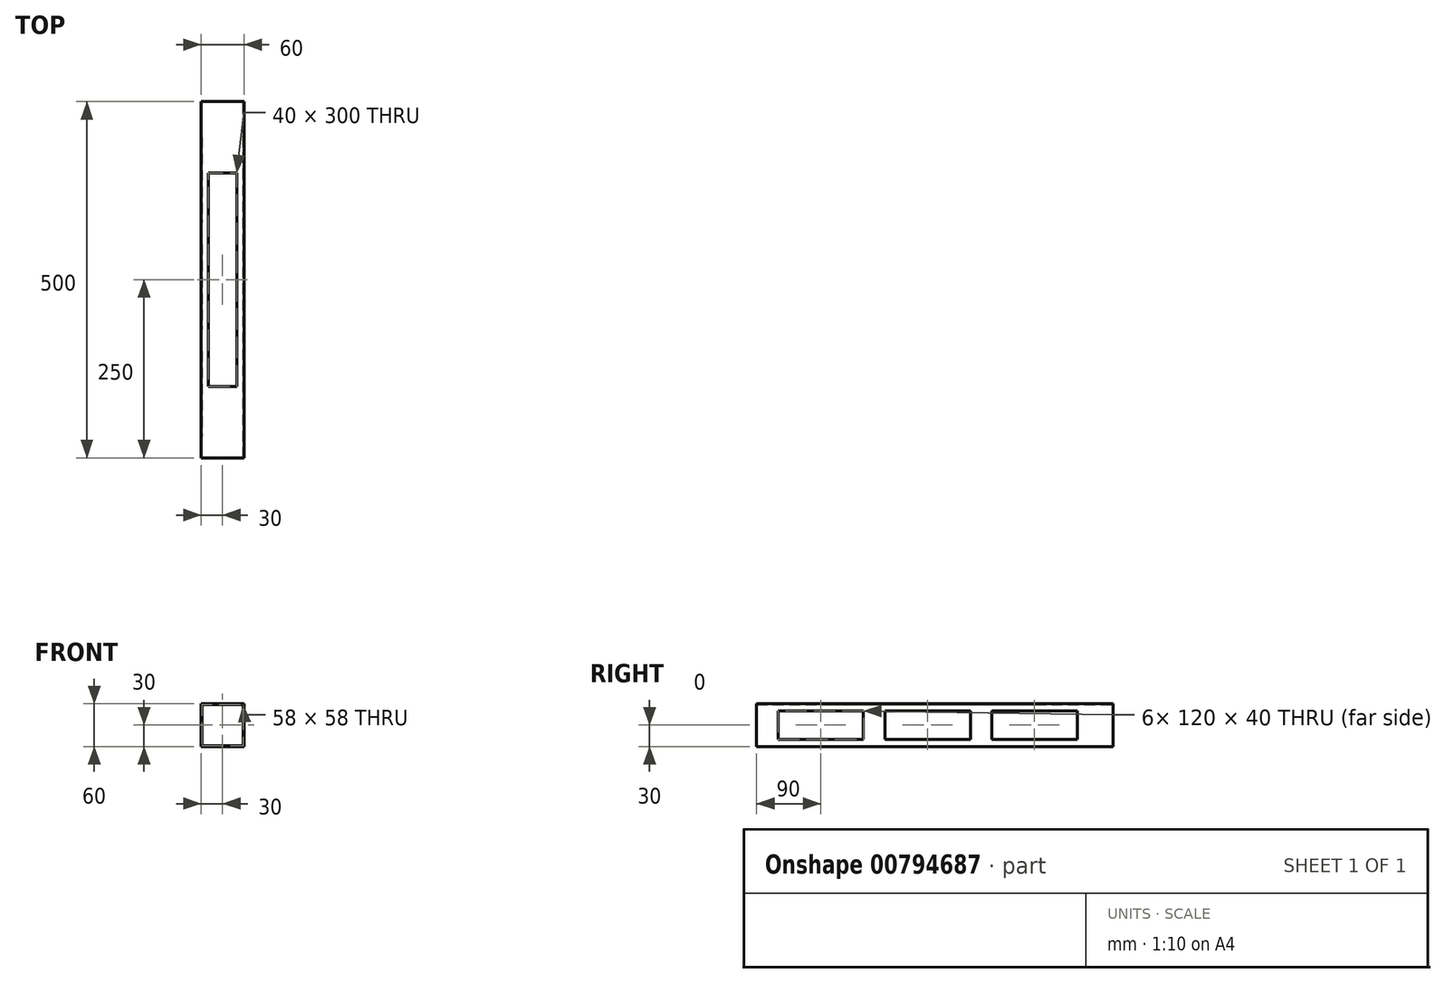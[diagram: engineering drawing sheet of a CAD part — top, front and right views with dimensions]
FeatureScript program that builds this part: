
annotation { "Feature Type Name" : "Feature", "Feature Type Description" : "" }
export const myFeature = defineFeature(function(context is Context, id is Id, definition is map)
    precondition{}
    {
        {
            var Q0;
            Q0=qCreatedBy(makeId("Front.planeOp"),FACE);
            var sketch = newSketch(context, id + "F0", { "sketchPlane" : qUnion([Q0])});
            skLineSegment(sketch, "E0.bottom", {"start": v(-30, -30) * mm, "end": v(30, -30) * mm});
            skLineSegment(sketch, "E0.top", {"start": v(-30, 30) * mm, "end": v(30, 30) * mm});
            skLineSegment(sketch, "E0.left", {"start": v(-30, -30) * mm, "end": v(-30, 30) * mm});
            skLineSegment(sketch, "E0.right", {"start": v(30, -30) * mm, "end": v(30, 30) * mm});
            skPoint(sketch, "E0.middle", {"position": v(0, 0) * mm});
            skLineSegment(sketch, "E1.bottom", {"start": v(-29, -29) * mm, "end": v(29, -29) * mm});
            skLineSegment(sketch, "E1.top", {"start": v(-29, 29) * mm, "end": v(29, 29) * mm});
            skLineSegment(sketch, "E1.left", {"start": v(-29, -29) * mm, "end": v(-29, 29) * mm});
            skLineSegment(sketch, "E1.right", {"start": v(29, -29) * mm, "end": v(29, 29) * mm});
            skSolve(sketch);
        }
        {
            var Q0;
            Q0=makeQuery(id+"F0.imprint","IMPRINT",FACE,{"disambiguationData":[TD([[makeQuery(id+"F0.imprint","IMPRINT",EDGE,{"derivedFrom":sQuery(id+"F0.wireOp",EDGE,"E0.bottom")}),1.0]])]});
            extrude(context, id + "F1", {"entities" : qUnion([Q0]), "depth" : 500 * mm, "offsetDistance" : 25 * mm});
        }
        {
            var Q0;
            Q0=makeQuery(id+"F1.opExtrude","SWEPT_FACE",FACE,{"disambiguationData":[OSD([sQuery(id+"F0.wireOp",EDGE,"E0.right")])]});
            var sketch = newSketch(context, id + "F2", { "sketchPlane" : qUnion([Q0])});
            skLineSegment(sketch, "E2.bottom", {"start": v(-470, 20) * mm, "end": v(-350, 20) * mm});
            skLineSegment(sketch, "E2.top", {"start": v(-470, -20) * mm, "end": v(-350, -20) * mm});
            skLineSegment(sketch, "E2.left", {"start": v(-470, 20) * mm, "end": v(-470, -20) * mm});
            skLineSegment(sketch, "E2.right", {"start": v(-350, 20) * mm, "end": v(-350, -20) * mm});
            skLineSegment(sketch, "E3.1.0.0", {"start": v(-320, 20) * mm, "end": v(-200, 20) * mm});
            skLineSegment(sketch, "E3.1.0.1", {"start": v(-200, 20) * mm, "end": v(-200, -20) * mm});
            skLineSegment(sketch, "E3.1.0.2", {"start": v(-320, -20) * mm, "end": v(-200, -20) * mm});
            skLineSegment(sketch, "E3.1.0.3", {"start": v(-320, 20) * mm, "end": v(-320, -20) * mm});
            skLineSegment(sketch, "E3.2.0.0", {"start": v(-170, 20) * mm, "end": v(-50, 20) * mm});
            skLineSegment(sketch, "E3.2.0.1", {"start": v(-50, 20) * mm, "end": v(-50, -20) * mm});
            skLineSegment(sketch, "E3.2.0.2", {"start": v(-170, -20) * mm, "end": v(-50, -20) * mm});
            skLineSegment(sketch, "E3.2.0.3", {"start": v(-170, 20) * mm, "end": v(-170, -20) * mm});
            skLineSegment(sketch, "E3.direction1", {"start": v(-470, 20) * mm, "end": v(-320, 20) * mm, "construction": true});
            skSolve(sketch);
        }
        {
            var Q0;
            Q0=makeQuery(id+"F2.imprint","IMPRINT",FACE,{"disambiguationData":[TD([[makeQuery(id+"F2.imprint","IMPRINT",EDGE,{"derivedFrom":sQuery(id+"F2.wireOp",EDGE,"E2.bottom")}),-1.0]])]});
            var Q1;
            Q1=makeQuery(id+"F2.imprint","IMPRINT",FACE,{"disambiguationData":[TD([[makeQuery(id+"F2.imprint","IMPRINT",EDGE,{"derivedFrom":sQuery(id+"F2.wireOp",EDGE,"E3.1.0.0")}),-1.0]])]});
            var Q2;
            Q2=makeQuery(id+"F2.imprint","IMPRINT",FACE,{"disambiguationData":[TD([[makeQuery(id+"F2.imprint","IMPRINT",EDGE,{"derivedFrom":sQuery(id+"F2.wireOp",EDGE,"E3.2.0.0")}),-1.0]])]});
            extrude(context, id + "F3", {"entities" : qUnion([Q0, Q1, Q2]), "operationType" : NewBodyOperationType.REMOVE, "oppositeDirection" : true, "depth" : 150 * mm, "offsetDistance" : 25 * mm});
        }
        {
            var Q0;
            Q0=makeQuery(id+"F1.opExtrude","SWEPT_FACE",FACE,{"disambiguationData":[OSD([sQuery(id+"F0.wireOp",EDGE,"E0.top")])]});
            var sketch = newSketch(context, id + "F4", { "sketchPlane" : qUnion([Q0])});
            skLineSegment(sketch, "E4.bottom", {"start": v(-20, -400) * mm, "end": v(20, -400) * mm});
            skLineSegment(sketch, "E4.top", {"start": v(-20, -100) * mm, "end": v(20, -100) * mm});
            skLineSegment(sketch, "E4.left", {"start": v(-20, -400) * mm, "end": v(-20, -100) * mm});
            skLineSegment(sketch, "E4.right", {"start": v(20, -400) * mm, "end": v(20, -100) * mm});
            skSolve(sketch);
        }
        {
            var Q0;
            Q0=makeQuery(id+"F4.imprint","IMPRINT",FACE,{"disambiguationData":[TD([[makeQuery(id+"F4.imprint","IMPRINT",EDGE,{"derivedFrom":sQuery(id+"F4.wireOp",EDGE,"E4.bottom")}),1.0]])]});
            extrude(context, id + "F5", {"entities" : qUnion([Q0]), "operationType" : NewBodyOperationType.REMOVE, "oppositeDirection" : true, "depth" : 25 * mm, "offsetDistance" : 25 * mm});
        }
    });
